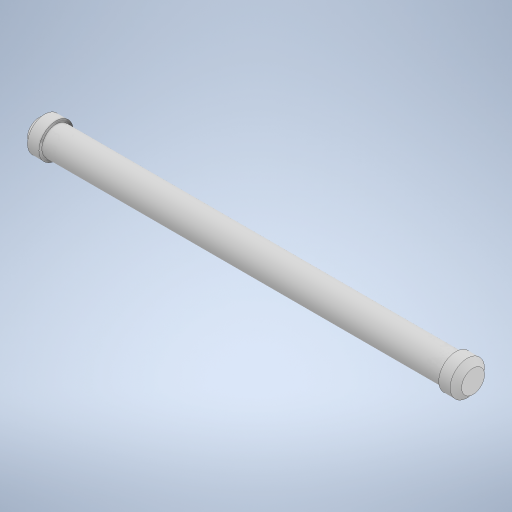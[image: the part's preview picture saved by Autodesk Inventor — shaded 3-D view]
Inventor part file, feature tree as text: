
AUTODESK INVENTOR PART (.ipt)
format: ipt  version: 2023 (Build 270158030, 158C)  size: 246,784 bytes
history: native  units: in
note: dims shown in document units (in); Inventor stores cm internally (conversion verified against a paired STEP export)
features: extrude x2, sketch x2, chamfer x1, mirror x1
ambient origin geometry x8: Origin, YZ Plane, XZ Plane, XY Plane, X Axis, Y Axis, Z Axis, Center Point
bodies: Solid1 (feature_tree)
feature tree (6):
  extrude  "Extrusion1"  Depth=3.5in TaperAngle=0.0deg
  extrude  "Extrusion2"  Depth=0.15in TaperAngle=0.0deg
  chamfer  "Chamfer1"  Distance=0.125in Angle=45.0deg
  mirror  "Mirror1"
  sketch  "Sketch1"  dims[d0=0.25in d1=3.5in d2=0.0in]
  sketch  "Sketch2"  dims[d3=0.3in d4=0.15in d5=0.0in d6=0.05in d7=0.125in d8=45.0deg]
